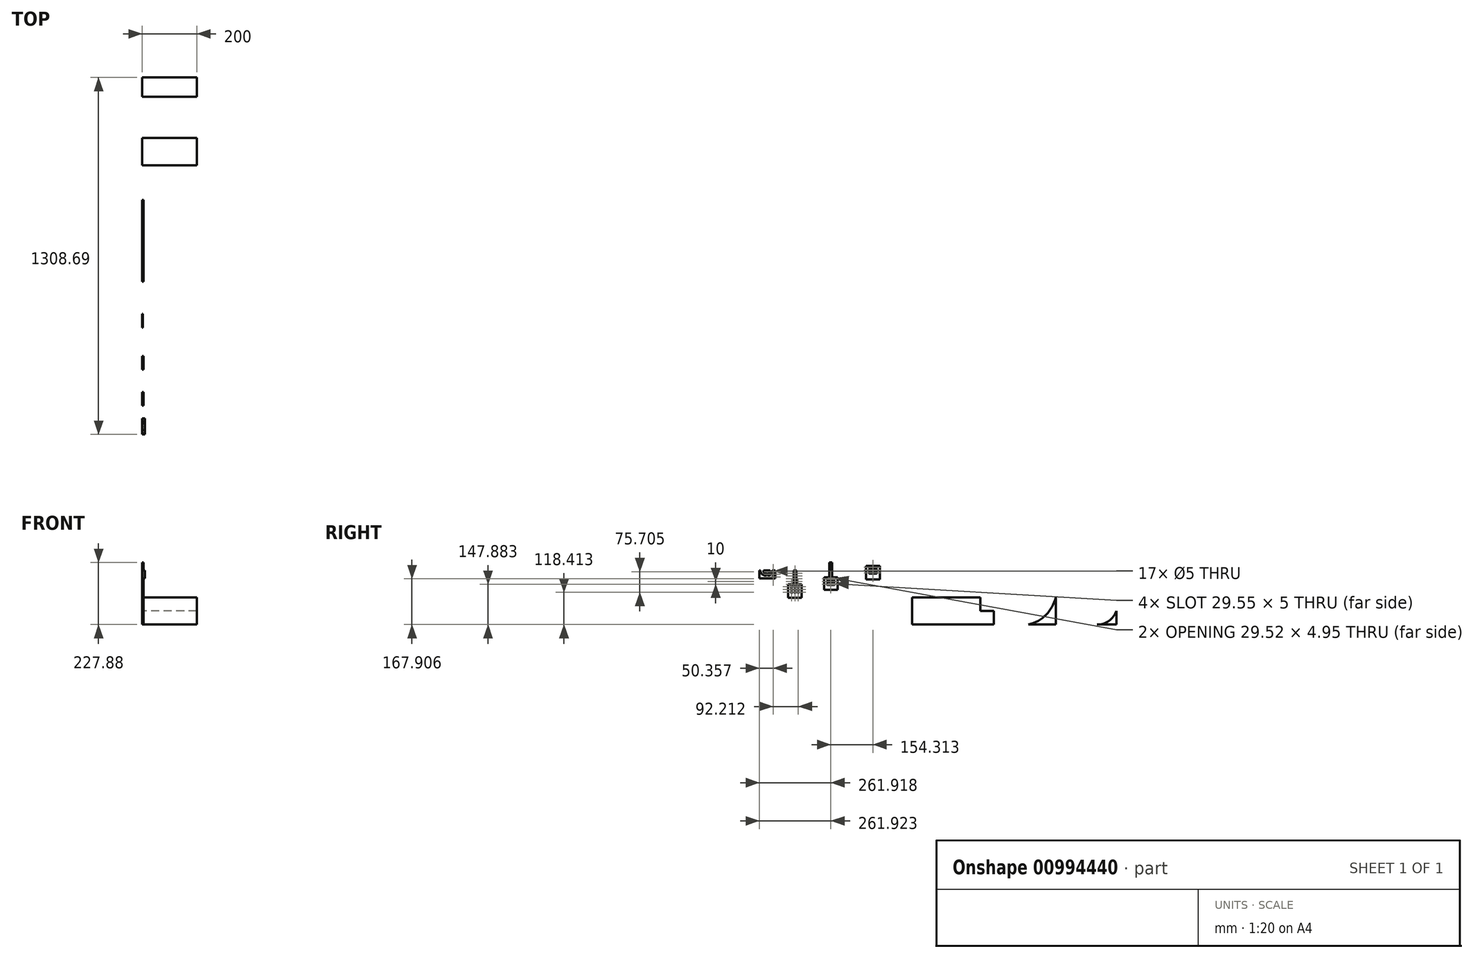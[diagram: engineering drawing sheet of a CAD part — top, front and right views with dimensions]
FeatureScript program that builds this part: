
annotation { "Feature Type Name" : "Feature", "Feature Type Description" : "" }
export const myFeature = defineFeature(function(context is Context, id is Id, definition is map)
    precondition{}
    {
        {
            var Q0;
            Q0=qCreatedBy(makeId("Right.planeOp"),FACE);
            var sketch = newSketch(context, id + "F0", { "sketchPlane" : qUnion([Q0])});
            skLineSegment(sketch, "E0.bottom", {"start": v(26.68, 70.65) * mm, "end": v(36.68, 70.65) * mm});
            skLineSegment(sketch, "E0.top", {"start": v(26.68, -29.35) * mm, "end": v(36.68, -29.35) * mm});
            skLineSegment(sketch, "E0.left", {"start": v(26.68, 70.65) * mm, "end": v(26.68, 20.65) * mm});
            skLineSegment(sketch, "E0.right", {"start": v(36.68, 70.65) * mm, "end": v(36.68, 20.65) * mm});
            skLineSegment(sketch, "E1", {"start": v(31.68, 70.65) * mm, "end": v(31.68, -29.35) * mm, "construction": true});
            skCircle(sketch, "E2", {"center": v(31.68, 60.65) * mm, "radius": 2.5 * mm});
            skCircle(sketch, "E3.0.1.0", {"center": v(31.68, 50.65) * mm, "radius": 2.5 * mm});
            skCircle(sketch, "E3.0.2.0", {"center": v(31.68, 40.65) * mm, "radius": 2.5 * mm});
            skCircle(sketch, "E3.0.3.0", {"center": v(31.68, 30.65) * mm, "radius": 2.5 * mm});
            skCircle(sketch, "E3.0.4.0", {"center": v(31.68, 20.65) * mm, "radius": 2.5 * mm});
            skCircle(sketch, "E3.0.5.0", {"center": v(31.68, 10.65) * mm, "radius": 2.5 * mm});
            skCircle(sketch, "E3.0.6.0", {"center": v(31.68, 0.65) * mm, "radius": 2.5 * mm});
            skCircle(sketch, "E3.0.7.0", {"center": v(31.68, -9.35) * mm, "radius": 2.5 * mm});
            skCircle(sketch, "E3.1.1.0", {"center": v(31.68, 50.65) * mm, "radius": 2.5 * mm});
            skCircle(sketch, "E3.1.2.0", {"center": v(31.68, 40.65) * mm, "radius": 2.5 * mm});
            skCircle(sketch, "E3.1.3.0", {"center": v(31.68, 30.65) * mm, "radius": 2.5 * mm});
            skCircle(sketch, "E3.1.4.0", {"center": v(31.68, 20.65) * mm, "radius": 2.5 * mm});
            skCircle(sketch, "E3.1.5.0", {"center": v(31.68, 10.65) * mm, "radius": 2.5 * mm});
            skCircle(sketch, "E3.1.6.0", {"center": v(31.68, 0.65) * mm, "radius": 2.5 * mm});
            skCircle(sketch, "E3.1.7.0", {"center": v(31.68, -9.35) * mm, "radius": 2.5 * mm});
            skCircle(sketch, "E3.2.1.0", {"center": v(31.68, 50.65) * mm, "radius": 2.5 * mm});
            skCircle(sketch, "E3.2.2.0", {"center": v(31.68, 40.65) * mm, "radius": 2.5 * mm});
            skCircle(sketch, "E3.2.3.0", {"center": v(31.68, 30.65) * mm, "radius": 2.5 * mm});
            skCircle(sketch, "E3.2.4.0", {"center": v(31.68, 20.65) * mm, "radius": 2.5 * mm});
            skCircle(sketch, "E3.2.5.0", {"center": v(31.68, 10.65) * mm, "radius": 2.5 * mm});
            skCircle(sketch, "E3.2.6.0", {"center": v(31.68, 0.65) * mm, "radius": 2.5 * mm});
            skCircle(sketch, "E3.2.7.0", {"center": v(31.68, -9.35) * mm, "radius": 2.5 * mm});
            skLineSegment(sketch, "E3.direction1", {"start": v(31.68, 60.65) * mm, "end": v(31.68, 60.65) * mm});
            skLineSegment(sketch, "E3.direction2", {"start": v(31.68, 60.65) * mm, "end": v(31.68, 50.65) * mm, "construction": true});
            skLineSegment(sketch, "E4.bottom", {"start": v(-45.8, 71.36) * mm, "end": v(-52.04, 71.36) * mm});
            skCircle(sketch, "E5.MirrorC", {"center": v(-48.3, 66.36) * mm, "radius": 2.5 * mm});
            skLineSegment(sketch, "E6.MirrorCS", {"start": v(-45.8, 41.36) * mm, "end": v(-80.75, 41.36) * mm, "construction": true});
            skLineSegment(sketch, "E7", {"start": v(-80.75, 41.36) * mm, "end": v(-45.8, 41.36) * mm});
            skCircle(sketch, "E8.MirrorC", {"center": v(-48.3, 47.25) * mm, "radius": 2.5 * mm});
            skPoint(sketch, "E9.end.orphan", {"position": v(-83.65, 61.36) * mm});
            skPoint(sketch, "E9.start.orphan", {"position": v(-45.8, 61.36) * mm});
            skArc(sketch, "E10", {"start": v(-65.8, 60.64) * mm, "mid": v(-69.54, 56.89) * mm, "end": v(-65.78, 53.14) * mm});
            skArc(sketch, "E11", {"start": v(-75.8, 53.14) * mm, "mid": v(-72.04, 56.89) * mm, "end": v(-75.8, 60.64) * mm});
            skLineSegment(sketch, "E12", {"start": v(-93.65, 41.36) * mm, "end": v(-80.75, 41.36) * mm});
            skPoint(sketch, "E13.start.orphan", {"position": v(-83.65, 51.36) * mm});
            skLineSegment(sketch, "E14", {"start": v(-75.8, 60.64) * mm, "end": v(-79.04, 60.64) * mm});
            skArc(sketch, "E15", {"start": v(-83.65, 71.36) * mm, "mid": v(-83.33, 65.15) * mm, "end": v(-79.04, 60.64) * mm});
            skLineSegment(sketch, "E16", {"start": v(-93.65, 71.36) * mm, "end": v(-98.65, 71.36) * mm});
            skLineSegment(sketch, "E17", {"start": v(-98.65, 71.36) * mm, "end": v(-98.65, 41.36) * mm});
            skLineSegment(sketch, "E18", {"start": v(-98.65, 41.36) * mm, "end": v(-93.65, 41.36) * mm});
            skLineSegment(sketch, "E19", {"start": v(-75.8, 53.14) * mm, "end": v(-82.66, 53.14) * mm});
            skPoint(sketch, "E20.orphan", {"position": v(-75.8, 52.8) * mm});
            skArc(sketch, "E21", {"start": v(-95.15, 71.36) * mm, "mid": v(-91.6, 60.4) * mm, "end": v(-82.66, 53.14) * mm});
            skLineSegment(sketch, "E22", {"start": v(-65.8, 60.64) * mm, "end": v(-61.27, 60.64) * mm});
            skPoint(sketch, "E22.startSnap0", {"position": v(-77.41, 60.64) * mm});
            skLineSegment(sketch, "E23", {"start": v(-65.78, 53.14) * mm, "end": v(-60.18, 53.15) * mm});
            skPoint(sketch, "E23.startSnap0", {"position": v(-79.23, 53.14) * mm});
            skArc(sketch, "E24", {"start": v(-61.27, 60.64) * mm, "mid": v(-59.27, 65.81) * mm, "end": v(-59.09, 71.36) * mm});
            skLineSegment(sketch, "E25", {"start": v(-45.8, 71.36) * mm, "end": v(-40.8, 71.36) * mm});
            skLineSegment(sketch, "E26", {"start": v(-40.8, 71.36) * mm, "end": v(-40.8, 41.36) * mm});
            skLineSegment(sketch, "E27", {"start": v(-40.8, 41.36) * mm, "end": v(-45.8, 41.36) * mm});
            skArc(sketch, "E28", {"start": v(-60.18, 53.15) * mm, "mid": v(-53.95, 61.3) * mm, "end": v(-52.04, 71.36) * mm});
            skPoint(sketch, "E29.orphan", {"position": v(-60.18, 60.64) * mm});
            skCircle(sketch, "E30", {"center": v(-48.3, 57.25) * mm, "radius": 2.5 * mm});
            skPoint(sketch, "E31.orphan", {"position": v(-45.8, 51.36) * mm});
            skLineSegment(sketch, "E32.trimOffspring", {"start": v(-59.09, 71.36) * mm, "end": v(-83.65, 71.36) * mm});
            skLineSegment(sketch, "E33", {"start": v(36.68, -29.35) * mm, "end": v(56.68, -29.35) * mm});
            skLineSegment(sketch, "E34", {"start": v(56.68, -29.35) * mm, "end": v(56.68, 10.65) * mm});
            skLineSegment(sketch, "E35", {"start": v(56.68, 10.65) * mm, "end": v(56.68, 20.65) * mm});
            skLineSegment(sketch, "E36", {"start": v(56.68, 20.65) * mm, "end": v(36.68, 20.65) * mm});
            skLineSegment(sketch, "E37", {"start": v(26.68, -29.35) * mm, "end": v(6.68, -29.35) * mm});
            skLineSegment(sketch, "E38", {"start": v(6.68, -29.35) * mm, "end": v(6.68, 20.65) * mm});
            skLineSegment(sketch, "E39", {"start": v(6.68, 20.65) * mm, "end": v(26.68, 20.65) * mm});
            skCircle(sketch, "E40", {"center": v(43.92, -9.35) * mm, "radius": 2.5 * mm});
            skCircle(sketch, "E41", {"center": v(43.92, 0.65) * mm, "radius": 2.5 * mm});
            skCircle(sketch, "E42", {"center": v(43.92, 10.65) * mm, "radius": 2.5 * mm});
            skCircle(sketch, "E43.MirrorC", {"center": v(19.45, 10.65) * mm, "radius": 2.5 * mm});
            skCircle(sketch, "E44.MirrorC", {"center": v(19.45, 0.65) * mm, "radius": 2.5 * mm});
            skCircle(sketch, "E45.MirrorC", {"center": v(19.45, -9.35) * mm, "radius": 2.5 * mm});
            skLineSegment(sketch, "E46.bottom", {"start": v(158.27, 100.12) * mm, "end": v(168.27, 100.12) * mm});
            skLineSegment(sketch, "E46.top", {"start": v(158.27, 0.12) * mm, "end": v(168.27, 0.12) * mm});
            skLineSegment(sketch, "E46.left", {"start": v(158.27, 100.12) * mm, "end": v(158.27, 45.63) * mm});
            skLineSegment(sketch, "E46.right", {"start": v(168.27, 100.12) * mm, "end": v(168.27, 45.63) * mm});
            skArc(sketch, "E47", {"start": v(165.77, 90.12) * mm, "mid": v(163.27, 92.62) * mm, "end": v(160.77, 90.12) * mm});
            skArc(sketch, "E48.0.3.0", {"start": v(160.77, 60.12) * mm, "mid": v(163.27, 57.62) * mm, "end": v(165.77, 60.12) * mm});
            skLineSegment(sketch, "E48.0.7.0", {"start": v(163.27, 17.62) * mm, "end": v(163.27, 17.62) * mm});
            skArc(sketch, "E48.1.3.0", {"start": v(160.77, 60.12) * mm, "mid": v(163.27, 57.62) * mm, "end": v(165.77, 60.12) * mm});
            skArc(sketch, "E48.1.5.0", {"start": v(163.42, 42.62) * mm, "mid": v(163.27, 42.62) * mm, "end": v(163.12, 42.62) * mm});
            skLineSegment(sketch, "E48.1.7.0", {"start": v(163.27, 17.62) * mm, "end": v(163.27, 17.62) * mm});
            skArc(sketch, "E48.2.3.0", {"start": v(160.77, 60.12) * mm, "mid": v(163.27, 57.62) * mm, "end": v(165.77, 60.12) * mm});
            skLineSegment(sketch, "E48.2.7.0", {"start": v(163.27, 17.62) * mm, "end": v(163.27, 17.62) * mm});
            skLineSegment(sketch, "E48.direction1", {"start": v(163.27, 90.12) * mm, "end": v(163.27, 90.12) * mm});
            skLineSegment(sketch, "E49", {"start": v(168.27, 0.12) * mm, "end": v(188.27, 0.12) * mm});
            skLineSegment(sketch, "E50", {"start": v(188.27, 0.12) * mm, "end": v(188.27, 50.12) * mm});
            skLineSegment(sketch, "E51", {"start": v(188.27, 45.63) * mm, "end": v(188.27, 50.12) * mm});
            skLineSegment(sketch, "E52", {"start": v(188.27, 45.63) * mm, "end": v(168.27, 45.63) * mm});
            skLineSegment(sketch, "E53", {"start": v(158.27, 0.12) * mm, "end": v(138.27, 0.12) * mm});
            skLineSegment(sketch, "E54", {"start": v(138.27, 0.12) * mm, "end": v(138.27, 45.63) * mm});
            skLineSegment(sketch, "E55", {"start": v(138.27, 45.63) * mm, "end": v(158.27, 45.63) * mm});
            skArc(sketch, "E56", {"start": v(175.55, 17.62) * mm, "mid": v(178.05, 20.12) * mm, "end": v(175.55, 22.62) * mm});
            skArc(sketch, "E57", {"start": v(175.55, 27.62) * mm, "mid": v(178.05, 30.12) * mm, "end": v(175.55, 32.62) * mm});
            skArc(sketch, "E58", {"start": v(174.98, 37.69) * mm, "mid": v(178.03, 39.84) * mm, "end": v(175.55, 42.62) * mm});
            skArc(sketch, "E59.MirrorC", {"start": v(151.56, 37.69) * mm, "mid": v(148.5, 39.94) * mm, "end": v(151.2, 42.61) * mm});
            skArc(sketch, "E60.MirrorC", {"start": v(151, 27.62) * mm, "mid": v(148.5, 30.12) * mm, "end": v(151, 32.62) * mm});
            skArc(sketch, "E61.MirrorC", {"start": v(151, 17.62) * mm, "mid": v(148.5, 20.12) * mm, "end": v(151, 22.62) * mm});
            skLineSegment(sketch, "E62", {"start": v(150.8, 42.61) * mm, "end": v(175.55, 42.62) * mm});
            skLineSegment(sketch, "E63", {"start": v(151, 37.69) * mm, "end": v(174.98, 37.69) * mm});
            skPoint(sketch, "E64.orphan", {"position": v(151.56, 37.69) * mm});
            skPoint(sketch, "E48.0.5.0.center.orphan", {"position": v(163.31, 40.12) * mm});
            skLineSegment(sketch, "E65", {"start": v(151, 32.62) * mm, "end": v(175.55, 32.62) * mm});
            skPoint(sketch, "E48.0.6.0.center.orphan", {"position": v(163.27, 30.12) * mm});
            skLineSegment(sketch, "E66", {"start": v(151, 27.62) * mm, "end": v(175.55, 27.62) * mm});
            skLineSegment(sketch, "E67.trimOffspring", {"start": v(163.27, 20.12) * mm, "end": v(163.27, 0.12) * mm, "construction": true});
            skLineSegment(sketch, "E68", {"start": v(151, 22.62) * mm, "end": v(175.55, 22.62) * mm});
            skLineSegment(sketch, "E69", {"start": v(151, 17.62) * mm, "end": v(175.55, 17.62) * mm});
            skLineSegment(sketch, "E70", {"start": v(165.77, 90.12) * mm, "end": v(165.77, 60.12) * mm});
            skLineSegment(sketch, "E71", {"start": v(160.77, 90.12) * mm, "end": v(160.77, 60.12) * mm});
            skPoint(sketch, "E72.orphan", {"position": v(163.27, 100.12) * mm});
            skLineSegment(sketch, "E73.trimOffspring", {"start": v(163.27, 42.62) * mm, "end": v(163.27, 42.62) * mm, "construction": true});
            skLineSegment(sketch, "E74.top", {"start": v(312.59, 37.41) * mm, "end": v(322.59, 37.41) * mm});
            skLineSegment(sketch, "E75.0.7.0", {"start": v(317.59, 59.41) * mm, "end": v(317.59, 59.41) * mm});
            skArc(sketch, "E75.1.5.0", {"start": v(317.73, 84.4) * mm, "mid": v(317.59, 84.41) * mm, "end": v(317.44, 84.4) * mm});
            skLineSegment(sketch, "E75.1.7.0", {"start": v(317.59, 59.41) * mm, "end": v(317.59, 59.41) * mm});
            skLineSegment(sketch, "E75.2.7.0", {"start": v(317.59, 59.41) * mm, "end": v(317.59, 59.41) * mm});
            skLineSegment(sketch, "E76", {"start": v(322.59, 37.41) * mm, "end": v(342.59, 37.41) * mm});
            skLineSegment(sketch, "E77", {"start": v(342.59, 37.41) * mm, "end": v(342.59, 77.41) * mm});
            skLineSegment(sketch, "E78", {"start": v(342.59, 77.41) * mm, "end": v(342.59, 87.41) * mm});
            skLineSegment(sketch, "E79", {"start": v(342.59, 87.41) * mm, "end": v(322.59, 87.41) * mm});
            skLineSegment(sketch, "E80", {"start": v(312.59, 37.41) * mm, "end": v(292.59, 37.41) * mm});
            skLineSegment(sketch, "E81", {"start": v(292.59, 37.41) * mm, "end": v(292.59, 87.41) * mm});
            skLineSegment(sketch, "E82", {"start": v(292.59, 87.41) * mm, "end": v(312.59, 87.41) * mm});
            skArc(sketch, "E83", {"start": v(329.86, 59.41) * mm, "mid": v(332.36, 61.91) * mm, "end": v(329.86, 64.41) * mm});
            skArc(sketch, "E84", {"start": v(329.86, 69.41) * mm, "mid": v(332.36, 71.91) * mm, "end": v(329.86, 74.41) * mm});
            skArc(sketch, "E85", {"start": v(329.3, 79.48) * mm, "mid": v(332.34, 81.63) * mm, "end": v(329.86, 84.41) * mm});
            skArc(sketch, "E86.MirrorC", {"start": v(305.88, 79.48) * mm, "mid": v(302.82, 81.73) * mm, "end": v(305.52, 84.4) * mm});
            skArc(sketch, "E87.MirrorC", {"start": v(305.31, 69.41) * mm, "mid": v(302.81, 71.91) * mm, "end": v(305.31, 74.41) * mm});
            skArc(sketch, "E88.MirrorC", {"start": v(305.31, 59.41) * mm, "mid": v(302.81, 61.91) * mm, "end": v(305.31, 64.41) * mm});
            skLineSegment(sketch, "E89", {"start": v(305.1, 84.4) * mm, "end": v(329.86, 84.41) * mm});
            skLineSegment(sketch, "E90", {"start": v(305.31, 79.48) * mm, "end": v(329.3, 79.48) * mm});
            skPoint(sketch, "E91.orphan", {"position": v(305.88, 79.48) * mm});
            skPoint(sketch, "E75.0.5.0.center.orphan", {"position": v(317.62, 81.91) * mm});
            skLineSegment(sketch, "E92", {"start": v(305.31, 74.41) * mm, "end": v(329.86, 74.41) * mm});
            skPoint(sketch, "E75.0.6.0.center.orphan", {"position": v(317.59, 71.91) * mm});
            skLineSegment(sketch, "E93", {"start": v(305.31, 69.41) * mm, "end": v(329.86, 69.41) * mm});
            skLineSegment(sketch, "E94.trimOffspring", {"start": v(317.59, 61.91) * mm, "end": v(317.59, 37.41) * mm, "construction": true});
            skLineSegment(sketch, "E95", {"start": v(305.31, 64.41) * mm, "end": v(329.86, 64.41) * mm});
            skLineSegment(sketch, "E96", {"start": v(305.31, 59.41) * mm, "end": v(329.86, 59.41) * mm});
            skLineSegment(sketch, "E97.trimOffspring", {"start": v(317.59, 84.41) * mm, "end": v(317.59, 84.4) * mm, "construction": true});
            skLineSegment(sketch, "E98", {"start": v(312.59, 87.41) * mm, "end": v(322.59, 87.41) * mm});
            skLineSegment(sketch, "E99.bottom", {"start": v(461.33, -27.76) * mm, "end": v(711.33, -27.76) * mm});
            skLineSegment(sketch, "E99.top", {"start": v(461.33, -127.76) * mm, "end": v(761.33, -127.76) * mm});
            skLineSegment(sketch, "E99.left", {"start": v(461.33, -27.76) * mm, "end": v(461.33, -127.76) * mm});
            skLineSegment(sketch, "E99.right", {"start": v(761.33, -77.76) * mm, "end": v(761.33, -127.76) * mm});
            skLineSegment(sketch, "E100", {"start": v(988.1, -27.76) * mm, "end": v(988.1, -127.76) * mm});
            skLineSegment(sketch, "E101", {"start": v(988.1, -127.76) * mm, "end": v(888.1, -127.76) * mm});
            skArc(sketch, "E102", {"start": v(888.1, -127.76) * mm, "mid": v(952.24, -91.9) * mm, "end": v(988.1, -27.76) * mm});
            skLineSegment(sketch, "E103", {"start": v(1140.04, -127.76) * mm, "end": v(1210.04, -127.76) * mm});
            skLineSegment(sketch, "E104", {"start": v(1210.04, -127.76) * mm, "end": v(1210.04, -77.76) * mm});
            skArc(sketch, "E105", {"start": v(1140.04, -127.76) * mm, "mid": v(1183.06, -113.98) * mm, "end": v(1210.04, -77.76) * mm});
            skLineSegment(sketch, "E106", {"start": v(761.33, -77.76) * mm, "end": v(711.33, -77.76) * mm});
            skLineSegment(sketch, "E107", {"start": v(711.33, -77.76) * mm, "end": v(711.33, -27.76) * mm});
            skPoint(sketch, "E108.orphan", {"position": v(761.33, -27.76) * mm});
            skSolve(sketch);
        }
        {
            var Q0;
            Q0=makeQuery(id+"F0.imprint","IMPRINT",FACE,{"disambiguationData":[TD([[makeQuery(id+"F0.imprint","IMPRINT",EDGE,{"derivedFrom":sQuery(id+"F0.wireOp",EDGE,"E4.bottom")}),1.0]])]});
            extrude(context, id + "F1", {"entities" : qUnion([Q0]), "depth" : 10 * mm, "offsetDistance" : 25 * mm});
        }
        {
            var Q0;
            Q0=makeQuery(id+"F0.imprint","IMPRINT",FACE,{"disambiguationData":[TD([[makeQuery(id+"F0.imprint","IMPRINT",EDGE,{"derivedFrom":sQuery(id+"F0.wireOp",EDGE,"E0.bottom")}),-1.0]])]});
            extrude(context, id + "F2", {"entities" : qUnion([Q0]), "depth" : 5 * mm, "offsetDistance" : 25 * mm});
        }
        {
            var Q0;
            Q0=makeQuery(id+"F0.imprint","IMPRINT",FACE,{"disambiguationData":[TD([[makeQuery(id+"F0.imprint","IMPRINT",EDGE,{"derivedFrom":sQuery(id+"F0.wireOp",EDGE,"E46.bottom")}),-1.0]])]});
            extrude(context, id + "F3", {"entities" : qUnion([Q0]), "depth" : 5 * mm, "offsetDistance" : 25 * mm});
        }
        {
            var Q0;
            Q0=makeQuery(id+"F0.imprint","IMPRINT",FACE,{"disambiguationData":[TD([[makeQuery(id+"F0.imprint","IMPRINT",EDGE,{"derivedFrom":sQuery(id+"F0.wireOp",EDGE,"E74.top")}),1.0]])]});
            extrude(context, id + "F4", {"entities" : qUnion([Q0]), "depth" : 2.5 * mm, "offsetDistance" : 25 * mm});
        }
        {
            var Q0;
            Q0=makeQuery(id+"F0.imprint","IMPRINT",FACE,{"disambiguationData":[TD([[makeQuery(id+"F0.imprint","IMPRINT",EDGE,{"derivedFrom":sQuery(id+"F0.wireOp",EDGE,"E99.bottom")}),-1.0]])]});
            extrude(context, id + "F5", {"entities" : qUnion([Q0]), "depth" : 5 * mm, "offsetDistance" : 25 * mm});
        }
        {
            var Q0;
            Q0=makeQuery(id+"F0.imprint","IMPRINT",FACE,{"disambiguationData":[TD([[makeQuery(id+"F0.imprint","IMPRINT",EDGE,{"derivedFrom":sQuery(id+"F0.wireOp",EDGE,"E100")}),-1.0]])]});
            extrude(context, id + "F6", {"entities" : qUnion([Q0]), "depth" : 200 * mm, "offsetDistance" : 25 * mm});
        }
        {
            var Q0;
            Q0=makeQuery(id+"F0.imprint","IMPRINT",FACE,{"disambiguationData":[TD([[makeQuery(id+"F0.imprint","IMPRINT",EDGE,{"derivedFrom":sQuery(id+"F0.wireOp",EDGE,"E103")}),1.0]])]});
            extrude(context, id + "F7", {"entities" : qUnion([Q0]), "depth" : 200 * mm, "offsetDistance" : 25 * mm});
        }
    });
